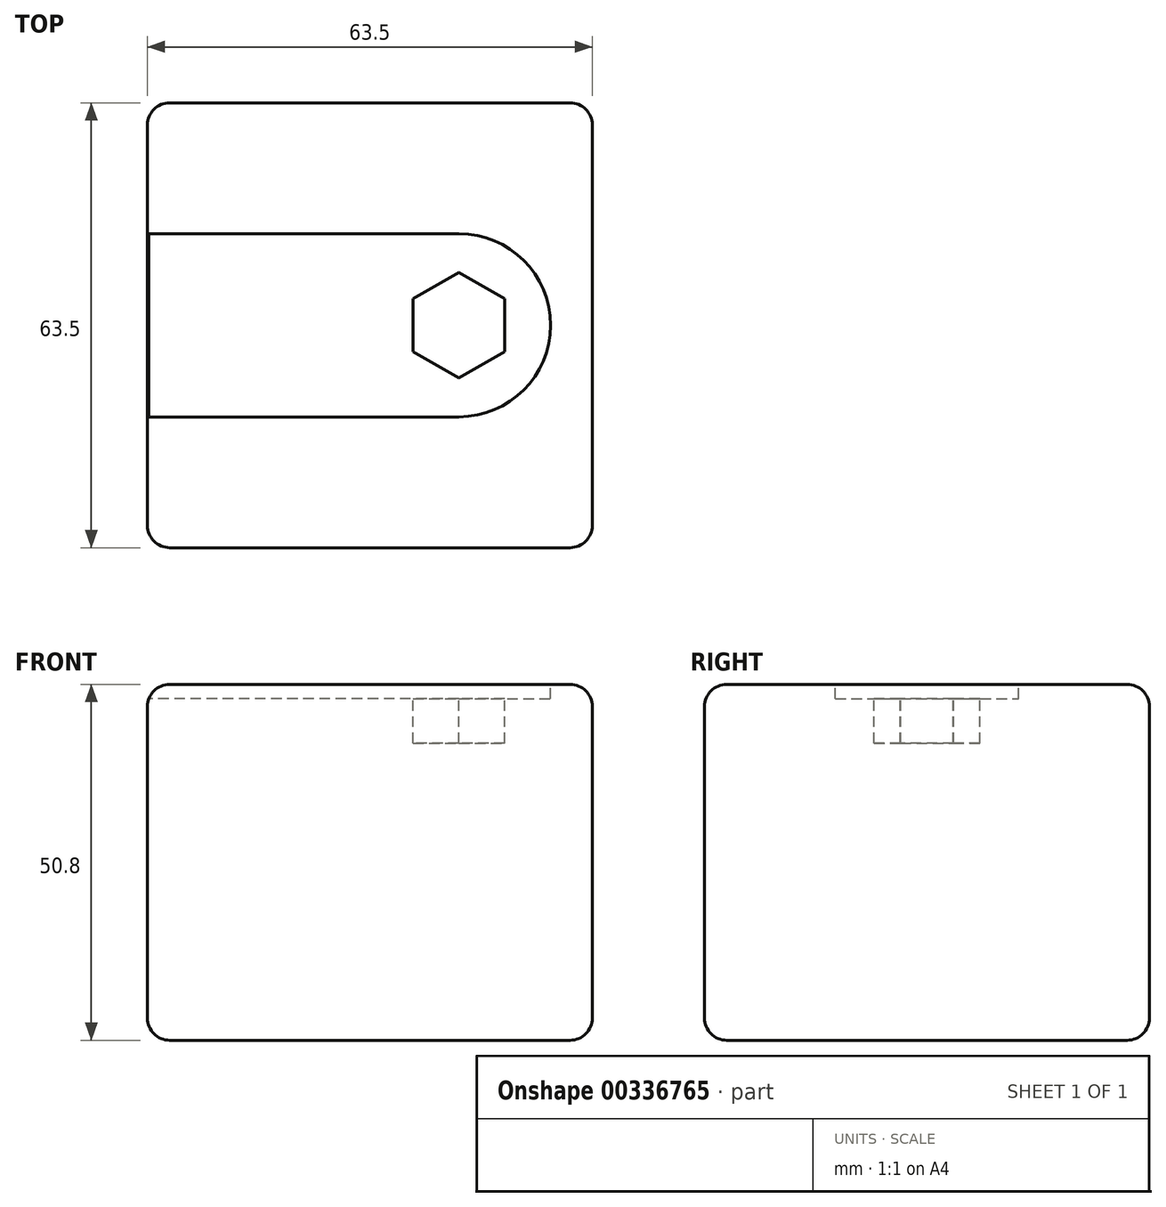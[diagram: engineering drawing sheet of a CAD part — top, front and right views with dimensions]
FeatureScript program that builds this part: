
annotation { "Feature Type Name" : "Feature", "Feature Type Description" : "" }
export const myFeature = defineFeature(function(context is Context, id is Id, definition is map)
    precondition{}
    {
        {
            var Q0;
            Q0=qCreatedBy(makeId("Top.planeOp"),FACE);
            var sketch = newSketch(context, id + "F0", { "sketchPlane" : qUnion([Q0])});
            skLineSegment(sketch, "E0.bottom", {"start": v(-31.75, -31.75) * mm, "end": v(31.75, -31.75) * mm});
            skLineSegment(sketch, "E0.top", {"start": v(-31.75, 31.75) * mm, "end": v(31.75, 31.75) * mm});
            skLineSegment(sketch, "E0.left", {"start": v(-31.75, -31.75) * mm, "end": v(-31.75, 31.75) * mm});
            skLineSegment(sketch, "E0.right", {"start": v(31.75, -31.75) * mm, "end": v(31.75, 31.75) * mm});
            skSolve(sketch);
        }
        {
            var Q0;
            Q0 = qSketchRegion(id + "F0", true);
            extrude(context, id + "F1", {"entities" : qUnion([Q0]), "depth" : 50.8 * mm});
        }
        {
            var Q0;
            Q0=makeQuery(id+"F1.opExtrude","CAP_FACE",FACE,{"disambiguationData":[OSD([sQuery(id+"F0.wireOp",EDGE,"E0.bottom"),sQuery(id+"F0.wireOp",EDGE,"E0.top"),sQuery(id+"F0.wireOp",EDGE,"E0.left"),sQuery(id+"F0.wireOp",EDGE,"E0.right")])],"isStart":false});
            var sketch = newSketch(context, id + "F2", { "sketchPlane" : qUnion([Q0])});
            skLineSegment(sketch, "E1.bottom", {"start": v(144.5, 48.44) * mm, "end": v(146.03, 48.44) * mm});
            skLineSegment(sketch, "E1.top", {"start": v(144.5, 54.4) * mm, "end": v(146.03, 54.4) * mm});
            skLineSegment(sketch, "E1.left", {"start": v(144.5, 48.44) * mm, "end": v(144.5, 54.4) * mm});
            skLineSegment(sketch, "E1.right", {"start": v(146.03, 48.44) * mm, "end": v(146.03, 54.4) * mm});
            skCircle(sketch, "E2.cCircle", {"center": v(12.7, 0) * mm, "radius": 6.54 * mm, "construction": true});
            skLineSegment(sketch, "E2.0", {"start": v(6.16, 3.77) * mm, "end": v(12.7, 7.55) * mm});
            skLineSegment(sketch, "E2.1", {"start": v(12.7, 7.55) * mm, "end": v(19.24, 3.78) * mm});
            skLineSegment(sketch, "E2.2", {"start": v(19.24, 3.78) * mm, "end": v(19.24, -3.77) * mm});
            skLineSegment(sketch, "E2.3", {"start": v(19.24, -3.77) * mm, "end": v(12.7, -7.55) * mm});
            skLineSegment(sketch, "E2.4", {"start": v(12.7, -7.55) * mm, "end": v(6.16, -3.78) * mm});
            skLineSegment(sketch, "E2.5", {"start": v(6.16, -3.78) * mm, "end": v(6.16, 3.77) * mm});
            skPoint(sketch, "E2.0.midPoint", {"position": v(9.42, 5.66) * mm});
            skSolve(sketch);
        }
        {
            var Q0;
            Q0=makeQuery(id+"F2.imprint","IMPRINT",FACE,{"disambiguationData":[TD([[makeQuery(id+"F2.imprint","IMPRINT",EDGE,{"derivedFrom":sQuery(id+"F2.wireOp",EDGE,"E2.0")}),1.0]])]});
            var sketch = newSketch(context, id + "F3", { "sketchPlane" : qUnion([Q0])});
            skArc(sketch, "E3", {"start": v(12.7, -13.08) * mm, "mid": v(25.78, 0) * mm, "end": v(12.7, 13.08) * mm});
            skLineSegment(sketch, "E4", {"start": v(12.7, 13.08) * mm, "end": v(-65.57, 13.08) * mm});
            skLineSegment(sketch, "E5", {"start": v(12.7, -13.08) * mm, "end": v(-58.2, -13.08) * mm});
            skLineSegment(sketch, "E6", {"start": v(-65.57, 13.08) * mm, "end": v(-58.2, -13.08) * mm});
            skSolve(sketch);
        }
        {
            var Q0;
            {var subQ1=sQuery(id+"F3.wireOp",EDGE,"E3");Q0=makeQuery(id+"F3.imprint","IMPRINT",FACE,{"disambiguationData":[TD([[makeQuery(id+"F3.imprint","IMPRINT",EDGE,{"derivedFrom":subQ1}),1.0]])]});}
            extrude(context, id + "F4", {"entities" : qUnion([Q0]), "operationType" : NewBodyOperationType.REMOVE, "oppositeDirection" : true, "depth" : 2.03 * mm});
        }
        {
            var Q0;
            Q0 = qSketchRegion(id + "F2", true);
            extrude(context, id + "F5", {"entities" : qUnion([Q0]), "operationType" : NewBodyOperationType.REMOVE, "oppositeDirection" : true, "depth" : 8.38 * mm});
        }
        {
            var Q0;
            Q0=makeQuery(id+"F1.opExtrude","SWEPT_EDGE",EDGE,{"disambiguationData":[OSD([sQuery(id+"F0.wireOp",EDGE,"E0.bottom"),sQuery(id+"F0.wireOp",EDGE,"E0.left")])]});
            var Q1;
            Q1=makeQuery(id+"F1.opExtrude","SWEPT_EDGE",EDGE,{"disambiguationData":[OSD([sQuery(id+"F0.wireOp",EDGE,"E0.bottom"),sQuery(id+"F0.wireOp",EDGE,"E0.right")])]});
            var Q2;
            Q2=makeQuery(id+"F1.opExtrude","SWEPT_EDGE",EDGE,{"disambiguationData":[OSD([sQuery(id+"F0.wireOp",EDGE,"E0.top"),sQuery(id+"F0.wireOp",EDGE,"E0.right")])]});
            var Q3;
            Q3=makeQuery(id+"F1.opExtrude","SWEPT_EDGE",EDGE,{"disambiguationData":[OSD([sQuery(id+"F0.wireOp",EDGE,"E0.top"),sQuery(id+"F0.wireOp",EDGE,"E0.left")])]});
            var Q4;
            Q4=makeQuery(id+"F1.opExtrude","CAP_EDGE",EDGE,{"disambiguationData":[OSD([sQuery(id+"F0.wireOp",EDGE,"E0.bottom")])],"isStart":false});
            var Q5;
            Q5=makeQuery(id+"F1.opExtrude","CAP_EDGE",EDGE,{"disambiguationData":[OSD([sQuery(id+"F0.wireOp",EDGE,"E0.right")])],"isStart":false});
            var Q6;
            Q6=makeQuery(id+"F1.opExtrude","CAP_EDGE",EDGE,{"disambiguationData":[OSD([sQuery(id+"F0.wireOp",EDGE,"E0.top")])],"isStart":false});
            var Q7;
            {var subQ0=sQuery(id+"F0.wireOp",EDGE,"E0.bottom");var subQ1=sQuery(id+"F0.wireOp",EDGE,"E0.left");Q7=makeQuery(id+"F4.boolean.opBoolean","SPLIT",EDGE,{"disambiguationData":[TD([makeQuery(id+"F1.opExtrude","SWEPT_FACE",FACE,{"disambiguationData":[OSD([subQ0])]})])],"derivedFrom":makeQuery(id+"F1.opExtrude","CAP_EDGE",EDGE,{"disambiguationData":[OSD([subQ1])],"isStart":false})});}
            var Q8;
            {var subQ0=sQuery(id+"F0.wireOp",EDGE,"E0.left");var subQ1=sQuery(id+"F0.wireOp",EDGE,"E0.top");Q8=makeQuery(id+"F4.boolean.opBoolean","SPLIT",EDGE,{"disambiguationData":[TD([makeQuery(id+"F1.opExtrude","SWEPT_FACE",FACE,{"disambiguationData":[OSD([subQ1])]})])],"derivedFrom":makeQuery(id+"F1.opExtrude","CAP_EDGE",EDGE,{"disambiguationData":[OSD([subQ0])],"isStart":false})});}
            var Q9;
            Q9=makeQuery(id+"F1.opExtrude","CAP_EDGE",EDGE,{"disambiguationData":[OSD([sQuery(id+"F0.wireOp",EDGE,"E0.bottom")])],"isStart":true});
            var Q10;
            Q10=makeQuery(id+"F1.opExtrude","CAP_EDGE",EDGE,{"disambiguationData":[OSD([sQuery(id+"F0.wireOp",EDGE,"E0.right")])],"isStart":true});
            var Q11;
            Q11=makeQuery(id+"F1.opExtrude","CAP_EDGE",EDGE,{"disambiguationData":[OSD([sQuery(id+"F0.wireOp",EDGE,"E0.left")])],"isStart":true});
            var Q12;
            Q12=makeQuery(id+"F1.opExtrude","CAP_EDGE",EDGE,{"disambiguationData":[OSD([sQuery(id+"F0.wireOp",EDGE,"E0.top")])],"isStart":true});
            fillet(context, id + "F6", {"entities" : qUnion([Q0, Q1, Q2, Q3, Q4, Q5, Q6, Q7, Q8, Q9, Q10, Q11, Q12]), "radius" : 3.17 * mm, "tangentPropagation" : true, "allowEdgeOverflow" : false});
        }
    });
